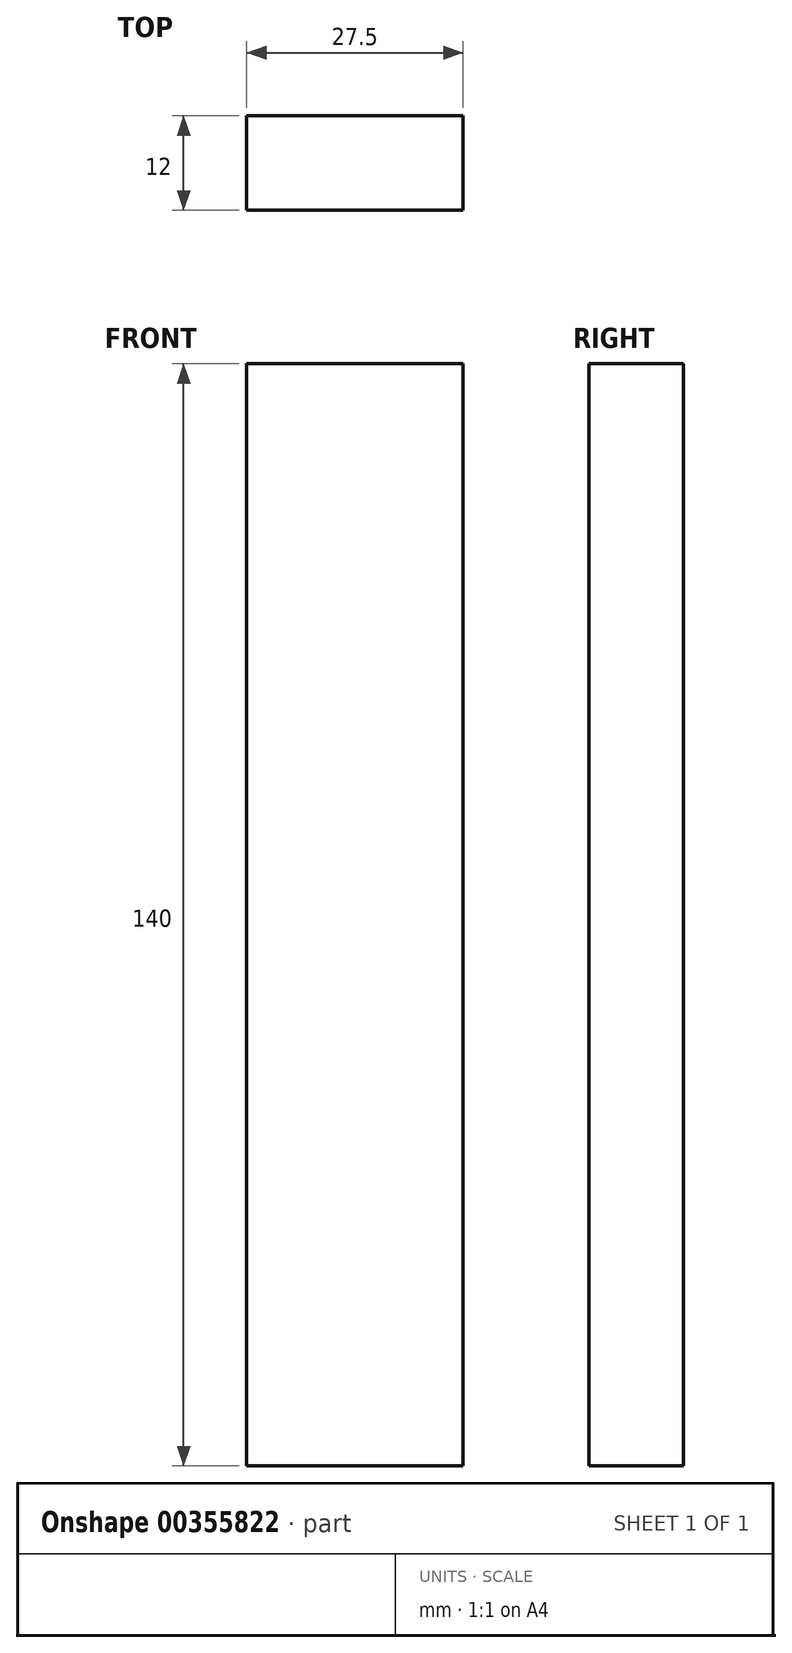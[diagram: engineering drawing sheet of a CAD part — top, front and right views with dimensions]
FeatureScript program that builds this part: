
annotation { "Feature Type Name" : "Feature", "Feature Type Description" : "" }
export const myFeature = defineFeature(function(context is Context, id is Id, definition is map)
    precondition{}
    {
        {
            var Q0;
            Q0=qCreatedBy(makeId("Front.planeOp"),FACE);
            var sketch = newSketch(context, id + "F0", { "sketchPlane" : qUnion([Q0])});
            skLineSegment(sketch, "E0", {"start": v(0, 0) * mm, "end": v(-13.75, 0) * mm, "construction": true});
            skLineSegment(sketch, "E1", {"start": v(-13.75, 0) * mm, "end": v(13.75, 0) * mm, "construction": true});
            skPoint(sketch, "E1.endSnap0", {"position": v(-6.88, 0) * mm});
            skLineSegment(sketch, "E2", {"start": v(-13.75, 0) * mm, "end": v(-13.75, 140) * mm});
            skLineSegment(sketch, "E3", {"start": v(-13.75, 140) * mm, "end": v(13.75, 140) * mm});
            skLineSegment(sketch, "E4", {"start": v(13.75, 140) * mm, "end": v(13.75, 0) * mm});
            skLineSegment(sketch, "E5", {"start": v(13.75, 0) * mm, "end": v(-13.75, 0) * mm});
            skSolve(sketch);
        }
        {
            var Q0;
            Q0=makeQuery(id+"F0.imprint","IMPRINT",FACE,{"disambiguationData":[TD([[makeQuery(id+"F0.imprint","IMPRINT",EDGE,{"derivedFrom":sQuery(id+"F0.wireOp",EDGE,"E2")}),-1.0]])]});
            extrude(context, id + "F1", {"entities" : qUnion([Q0]), "endBound" : BoundingType.SYMMETRIC, "depth" : 12 * mm});
        }
        {
            var Q0;
            Q0=makeQuery(id+"F1.opExtrude","SWEPT_FACE",FACE,{"disambiguationData":[OSD([sQuery(id+"F0.wireOp",EDGE,"E4")])]});
            cPlane(context, id + "F2", {"entities" : qUnion([Q0]), "cplaneType" : CPlaneType.OFFSET, "offset" : 0 * mm, "width" : 150 * mm, "height" : 150 * mm});
        }
    });
